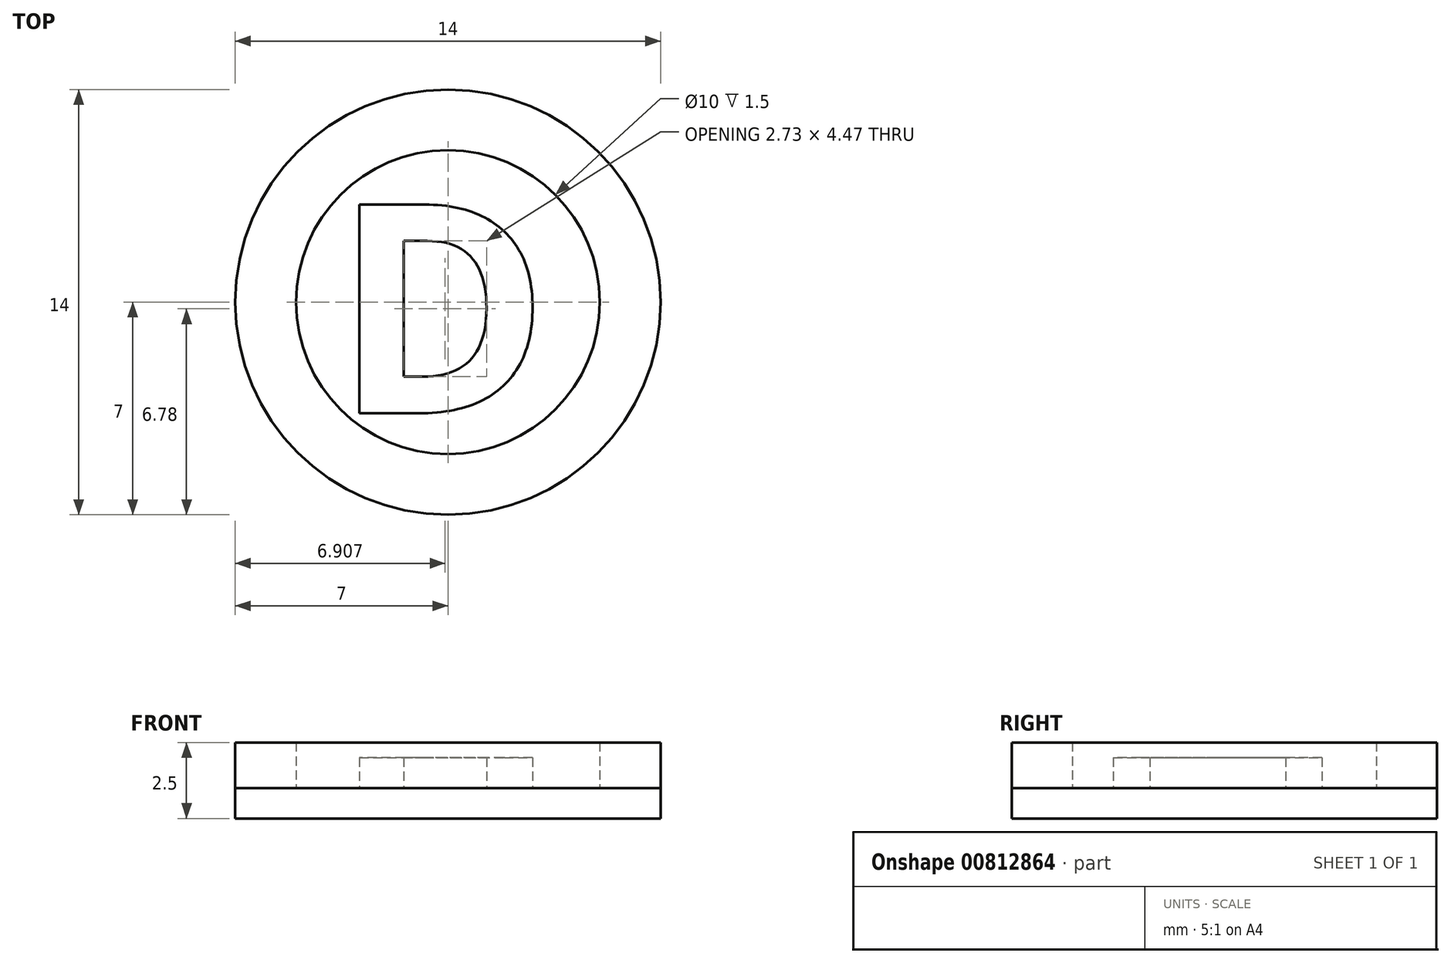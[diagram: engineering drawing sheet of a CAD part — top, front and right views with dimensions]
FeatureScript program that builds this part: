
annotation { "Feature Type Name" : "Feature", "Feature Type Description" : "" }
export const myFeature = defineFeature(function(context is Context, id is Id, definition is map)
    precondition{}
    {
        {
            var Q0;
            Q0=qCreatedBy(makeId("Top.planeOp"),FACE);
            var sketch = newSketch(context, id + "F0", { "sketchPlane" : qUnion([Q0])});
            skCircle(sketch, "E0", {"center": v(0, 0) * mm, "radius": 7 * mm});
            skCircle(sketch, "E1", {"center": v(0, 0) * mm, "radius": 5 * mm});
            skText(sketch, "E2", { "text": "D", "fontName": "OpenSans-Bold.ttf"});
            const initialGuessF0  = {"E2": [-0.00378, -0.00366, 1, 0, 0.00693]};
            skSetInitialGuess(sketch, initialGuessF0);
            skSolve(sketch);
        }
        {
            var Q0;
            Q0=makeQuery(id+"F0.imprint","IMPRINT",FACE,{"disambiguationData":[TD([[makeQuery(id+"F0.imprint","IMPRINT",EDGE,{"derivedFrom":sQuery(id+"F0.wireOp",EDGE,"E0")}),1.0]])]});
            var Q1;
            Q1=makeQuery(id+"F0.imprint","IMPRINT",FACE,{"disambiguationData":[TD([[makeQuery(id+"F0.imprint","IMPRINT",EDGE,{"derivedFrom":sQuery(id+"F0.wireOp",EDGE,"E1")}),1.0]])]});
            var Q2;
            Q2=makeQuery(id+"F0.imprint","IMPRINT",FACE,{"disambiguationData":[TD([[makeQuery(id+"F0.imprint","IMPRINT",EDGE,{"derivedFrom":sQuery(id+"F0.wireOp",EDGE,"E2.sketch_text.stroke-0")}),-1.0]])]});
            var Q3;
            Q3=makeQuery(id+"F0.imprint","IMPRINT",FACE,{"disambiguationData":[TD([[makeQuery(id+"F0.imprint","IMPRINT",EDGE,{"derivedFrom":sQuery(id+"F0.wireOp",EDGE,"E2.sketch_text.stroke-7")}),1.0]])]});
            extrude(context, id + "F1", {"entities" : qUnion([Q0, Q1, Q2, Q3]), "depth" : -1 * mm, "offsetDistance" : 25 * mm});
        }
        {
            var Q0;
            Q0=makeQuery(id+"F0.imprint","IMPRINT",FACE,{"disambiguationData":[TD([[makeQuery(id+"F0.imprint","IMPRINT",EDGE,{"derivedFrom":sQuery(id+"F0.wireOp",EDGE,"E0")}),1.0]])]});
            extrude(context, id + "F2", {"entities" : qUnion([Q0]), "depth" : 1.5 * mm, "offsetDistance" : 25 * mm});
        }
        {
            var Q0;
            Q0=makeQuery(id+"F0.imprint","IMPRINT",FACE,{"disambiguationData":[TD([[makeQuery(id+"F0.imprint","IMPRINT",EDGE,{"derivedFrom":sQuery(id+"F0.wireOp",EDGE,"E2.sketch_text.stroke-0")}),-1.0]])]});
            extrude(context, id + "F3", {"entities" : qUnion([Q0]), "depth" : 1 * mm, "offsetDistance" : 25 * mm});
        }
    });
